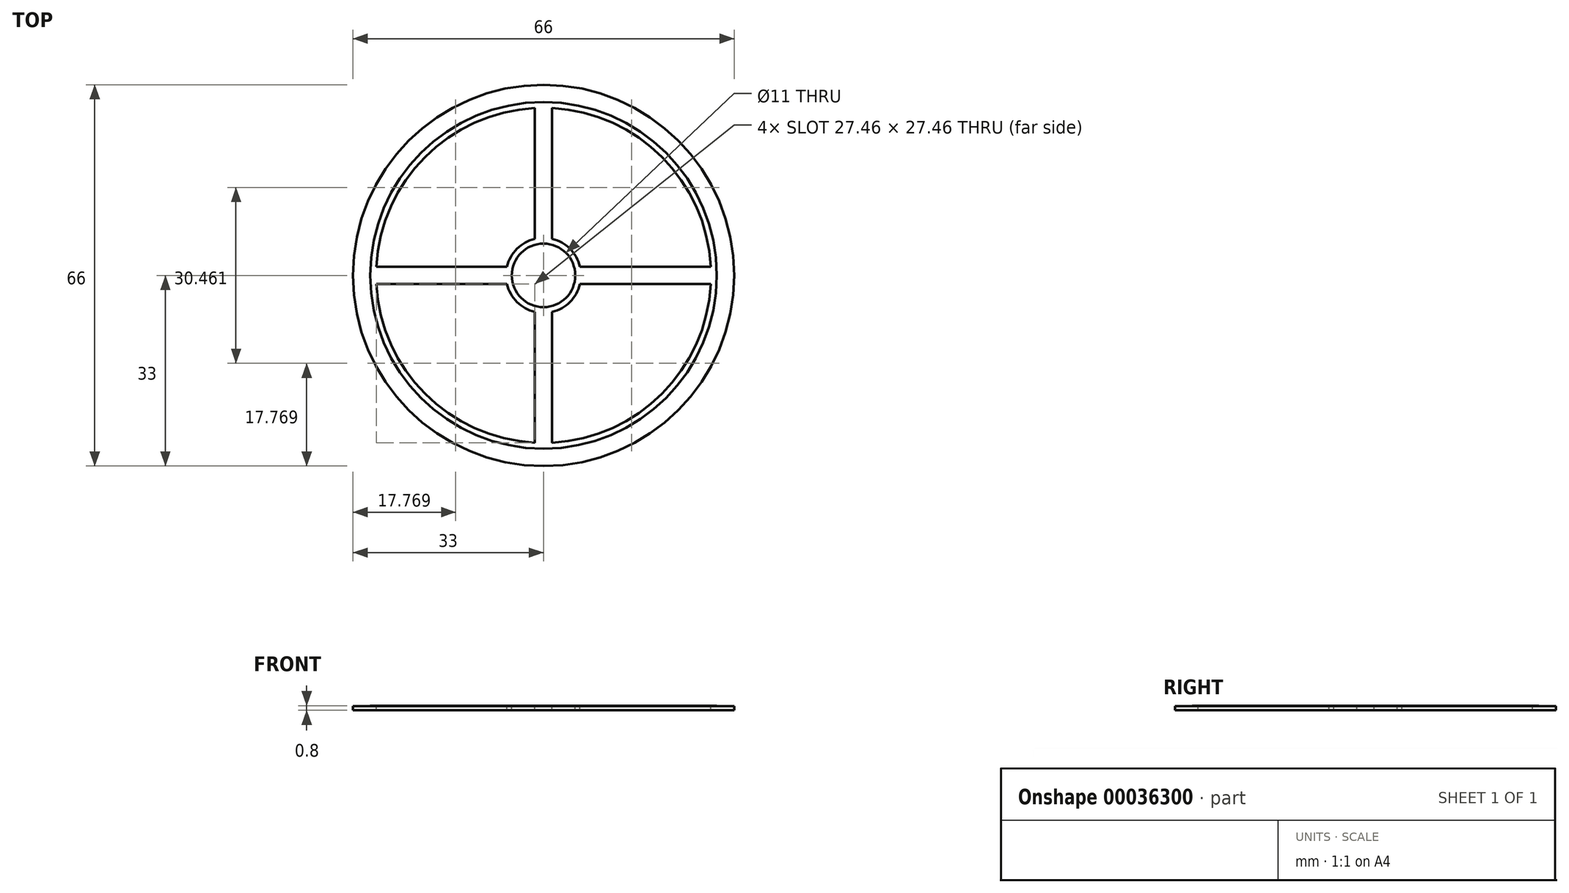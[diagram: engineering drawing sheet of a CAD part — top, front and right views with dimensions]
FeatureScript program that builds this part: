
annotation { "Feature Type Name" : "Feature", "Feature Type Description" : "" }
export const myFeature = defineFeature(function(context is Context, id is Id, definition is map)
    precondition{}
    {
        {
            var Q0;
            Q0=qCreatedBy(makeId("Top.planeOp"),FACE);
            var sketch = newSketch(context, id + "F0", { "sketchPlane" : qUnion([Q0])});
            skCircle(sketch, "E0", {"center": v(0, 0) * mm, "radius": 30 * mm});
            skSolve(sketch);
        }
        {
            var Q0;
            Q0=makeQuery(id+"F0.imprint","IMPRINT",FACE,{"disambiguationData":[TD([[makeQuery(id+"F0.imprint","IMPRINT",EDGE,{"derivedFrom":sQuery(id+"F0.wireOp",EDGE,"E0")}),1.0]])]});
            extrude(context, id + "F1", {"entities" : qUnion([Q0]), "depth" : 0.1 * mm});
        }
        {
            var Q0;
            Q0=makeQuery(id+"F1.opExtrude","CAP_FACE",FACE,{"disambiguationData":[OSD([sQuery(id+"F0.wireOp",EDGE,"E0")])],"isStart":false});
            var sketch = newSketch(context, id + "F2", { "sketchPlane" : qUnion([Q0])});
            skCircle(sketch, "E1", {"center": v(0, 0) * mm, "radius": 5.5 * mm});
            skSolve(sketch);
        }
        {
            var Q0;
            Q0=makeQuery(id+"F2.imprint","IMPRINT",FACE,{"disambiguationData":[TD([[makeQuery(id+"F2.imprint","IMPRINT",EDGE,{"derivedFrom":sQuery(id+"F2.wireOp",EDGE,"E1")}),1.0]])]});
            extrude(context, id + "F3", {"entities" : qUnion([Q0]), "operationType" : NewBodyOperationType.REMOVE, "endBound" : BoundingType.UP_TO_NEXT, "oppositeDirection" : true, "depth" : 1 * mm});
        }
        {
            var Q0;
            Q0=makeQuery(id+"F1.opExtrude","CAP_FACE",FACE,{"disambiguationData":[OSD([sQuery(id+"F0.wireOp",EDGE,"E0")])],"isStart":false});
            var sketch = newSketch(context, id + "F4", { "sketchPlane" : qUnion([Q0])});
            skCircle(sketch, "E2", {"center": v(0, 0) * mm, "radius": 29 * mm});
            skCircle(sketch, "E3", {"center": v(0, 0) * mm, "radius": 6.5 * mm});
            skLineSegment(sketch, "E4", {"start": v(0, -6.5) * mm, "end": v(0, -29) * mm, "construction": true});
            skLineSegment(sketch, "E5", {"start": v(-6.5, 0) * mm, "end": v(-29, 0) * mm, "construction": true});
            skLineSegment(sketch, "E6", {"start": v(0, 6.5) * mm, "end": v(0, 29) * mm, "construction": true});
            skLineSegment(sketch, "E7", {"start": v(6.5, 0) * mm, "end": v(29, 0) * mm, "construction": true});
            skLineSegment(sketch, "E8.0", {"start": v(1.5, 6.32) * mm, "end": v(1.5, 28.96) * mm});
            skLineSegment(sketch, "E9.0", {"start": v(-1.5, 6.32) * mm, "end": v(-1.5, 28.96) * mm});
            skLineSegment(sketch, "E10", {"start": v(1.5, -6.32) * mm, "end": v(1.5, -28.96) * mm});
            skLineSegment(sketch, "E11", {"start": v(-1.5, -6.32) * mm, "end": v(-1.5, -28.96) * mm});
            skLineSegment(sketch, "E12.0", {"start": v(6.32, 1.5) * mm, "end": v(28.96, 1.5) * mm});
            skLineSegment(sketch, "E13.0", {"start": v(6.32, -1.5) * mm, "end": v(28.96, -1.5) * mm});
            skLineSegment(sketch, "E14", {"start": v(-6.32, 1.5) * mm, "end": v(-28.96, 1.5) * mm});
            skLineSegment(sketch, "E15", {"start": v(-6.32, -1.5) * mm, "end": v(-28.96, -1.5) * mm});
            skSolve(sketch);
        }
        {
            var Q0;
            {var subQ1=sQuery(id+"F4.wireOp",EDGE,"E8.0");Q0=makeQuery(id+"F4.imprint","IMPRINT",FACE,{"disambiguationData":[TD([[makeQuery(id+"F4.imprint","IMPRINT",EDGE,{"derivedFrom":subQ1}),-1.0]])]});}
            var Q1;
            {var subQ2=sQuery(id+"F4.wireOp",EDGE,"E9.0");Q1=makeQuery(id+"F4.imprint","IMPRINT",FACE,{"disambiguationData":[TD([[makeQuery(id+"F4.imprint","IMPRINT",EDGE,{"derivedFrom":subQ2}),1.0]])]});}
            var Q2;
            {var subQ1=sQuery(id+"F4.wireOp",EDGE,"E11");Q2=makeQuery(id+"F4.imprint","IMPRINT",FACE,{"disambiguationData":[TD([[makeQuery(id+"F4.imprint","IMPRINT",EDGE,{"derivedFrom":subQ1}),-1.0]])]});}
            var Q3;
            {var subQ0=sQuery(id+"F4.wireOp",EDGE,"E10");Q3=makeQuery(id+"F4.imprint","IMPRINT",FACE,{"disambiguationData":[TD([[makeQuery(id+"F4.imprint","IMPRINT",EDGE,{"derivedFrom":subQ0}),1.0]])]});}
            extrude(context, id + "F5", {"entities" : qUnion([Q0, Q1, Q2, Q3]), "operationType" : NewBodyOperationType.REMOVE, "endBound" : BoundingType.UP_TO_NEXT, "oppositeDirection" : true, "depth" : 25 * mm});
        }
        {
            var Q0;
            Q0=makeQuery(id+"F1.opExtrude","CAP_FACE",FACE,{"disambiguationData":[OSD([sQuery(id+"F0.wireOp",EDGE,"E0")])],"isStart":true});
            var sketch = newSketch(context, id + "F6", { "sketchPlane" : qUnion([Q0])});
            skCircle(sketch, "E16", {"center": v(0, 0) * mm, "radius": 33 * mm});
            skSolve(sketch);
        }
        {
            var Q0;
            Q0=makeQuery(id+"F6.imprint","IMPRINT",FACE,{"disambiguationData":[TD([[makeQuery(id+"F6.imprint","IMPRINT",EDGE,{"derivedFrom":sQuery(id+"F6.wireOp",EDGE,"E16")}),1.0]])]});
            var Q1;
            {var subQ0=sQuery(id+"F0.wireOp",EDGE,"E0");Q1=makeQuery(id+"F6.imprint","IMPRINT",FACE,{"disambiguationData":[TD([[makeQuery(id+"F6.imprint","IMPRINT",EDGE,{"derivedFrom":makeQuery(id+"F1.opExtrude","CAP_EDGE",EDGE,{"disambiguationData":[OSD([subQ0])],"isStart":true})}),-1.0]])]});}
            extrude(context, id + "F7", {"entities" : qUnion([Q0, Q1]), "operationType" : NewBodyOperationType.ADD, "depth" : 0.7 * mm});
        }
    });
